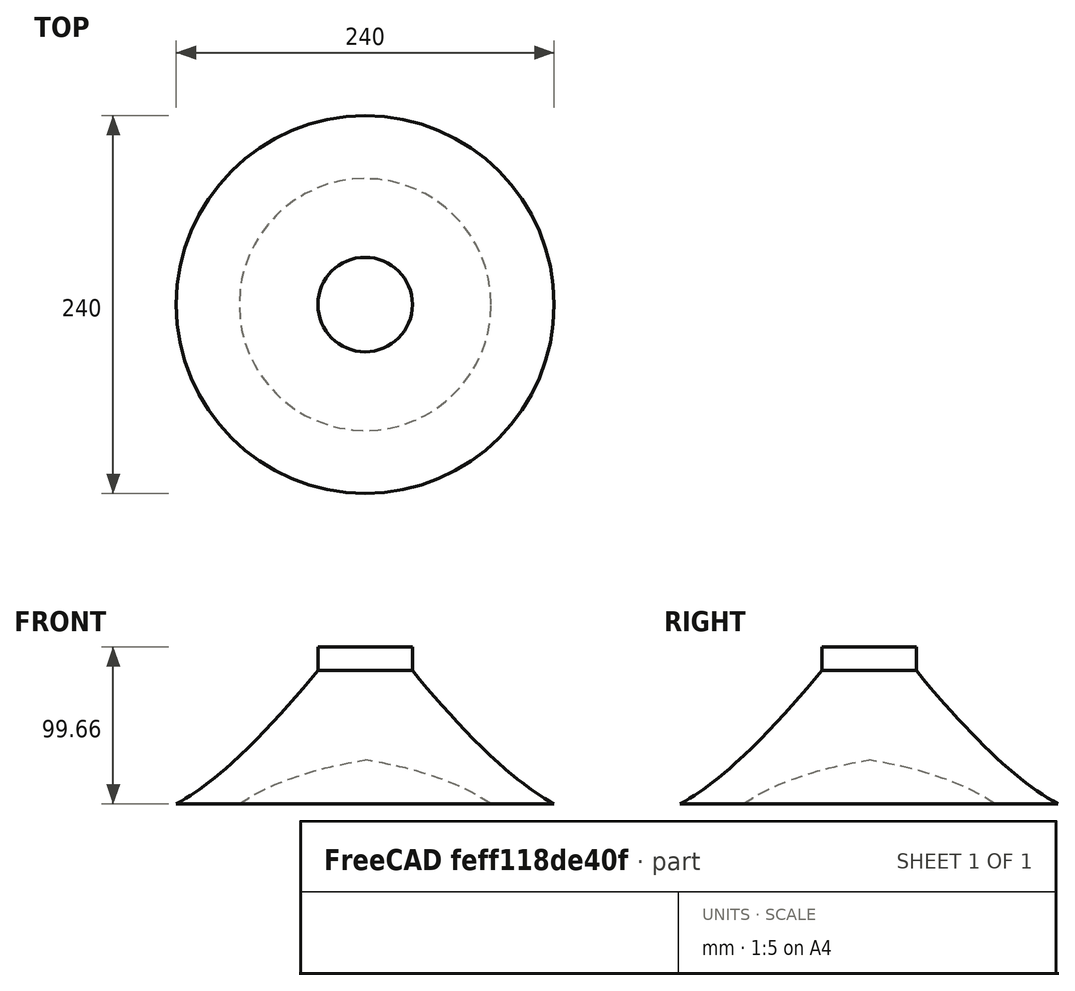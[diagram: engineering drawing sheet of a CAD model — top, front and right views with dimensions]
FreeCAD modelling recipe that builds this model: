
FCSTD DOCUMENT  (FreeCAD 0.20R29410 (Git))
Label: parte_baixo_1
License: All rights reserved
LicenseURL: http://en.wikipedia.org/wiki/All_rights_reserved
objects: Sketcher::SketchObject×1, PartDesign::Revolution×1, PartDesign::Body×1
note: 4 computed .brp shape members not serialized (recipe doc carries the construction recipe); baked Part::Feature solids carry a one-line shape summary decoded from their .brp

FEATURE [Sketcher::SketchObject] Sketch
  FullyConstrained = false
  MapMode = 5
  Placement = pos=(0,0,0) rot=(0.57735,0.57735,0.57735;2.0944rad)
  Support = -> [YZ_Plane]
  sketch-geometry (16):
    g0: Circle CenterX=30 CenterY=84.6645 CenterZ=0 NormalX=0 NormalY=0 NormalZ=1 AngleXU=0 Radius=1
    g1: Circle CenterX=83.0365 CenterY=20 CenterZ=0 NormalX=0 NormalY=0 NormalZ=1 AngleXU=0 Radius=1
    g2: Circle CenterX=120 CenterY=0 CenterZ=0 NormalX=0 NormalY=0 NormalZ=1 AngleXU=0 Radius=1
    g3: BSplineCurve PolesCount=3 KnotsCount=2 Degree=2 IsPeriodic=0
    g4: GeomPoint X=30 Y=84.6645 Z=0
    g5: GeomPoint X=120 Y=0 Z=0
    g6: Circle CenterX=80 CenterY=0 CenterZ=0 NormalX=0 NormalY=0 NormalZ=1 AngleXU=0 Radius=1
    g7: Circle CenterX=50 CenterY=20 CenterZ=0 NormalX=0 NormalY=0 NormalZ=1 AngleXU=0 Radius=1
    g8: Circle CenterX=0 CenterY=27.7845 CenterZ=0 NormalX=0 NormalY=0 NormalZ=1 AngleXU=0 Radius=1
    g9: BSplineCurve PolesCount=3 KnotsCount=2 Degree=2 IsPeriodic=0
    g10: GeomPoint X=80 Y=0 Z=0
    g11: GeomPoint X=0 Y=27.7845 Z=0
    g12: LineSegment StartX=120 StartY=0 StartZ=0 EndX=80 EndY=0 EndZ=0
    g13: LineSegment StartX=0 StartY=99.6645 StartZ=0 EndX=0 EndY=27.7845 EndZ=0
    g14: LineSegment StartX=30 StartY=84.6645 StartZ=0 EndX=30 EndY=99.6645 EndZ=0
    g15: LineSegment StartX=30 StartY=99.6645 StartZ=0 EndX=0 EndY=99.6645 EndZ=0
  constraints (31):
    c: PointOnObject(g3,g-1)
    c: PointOnObject(g13,g-2)
    c: Weight(g0) = 1
    c: Equal(g0,g1)
    c: Equal(g0,g2)
    c: InternalAlignment(g0,g3)
    c: InternalAlignment(g1,g3)
    c: InternalAlignment(g2,g3)
    c: InternalAlignment(g4,g3)
    c: InternalAlignment(g5,g3)
    c: Weight(g6) = 1
    c: Equal(g6,g7)
    c: Equal(g6,g8)
    c: InternalAlignment(g6,g9)
    c: InternalAlignment(g7,g9)
    c: InternalAlignment(g8,g9)
    c: InternalAlignment(g10,g9)
    c: InternalAlignment(g11,g9)
    c: Coincident(g12,g3)
    c: Horizontal(g12)
    c: Coincident(g13,g9)
    c: Vertical(g13)
    c: Distance(g12) = 40
    c: Coincident(g14,g3)
    c: Vertical(g14)
    c: Coincident(g14,g15)
    c: Coincident(g15,g13)
    c: Horizontal(g15)
    c: Distance(g14) = 15
    c: Distance(g15) = 30
    c: Distance(g13) = 71.88
FEATURE [PartDesign::Revolution] Revolution
  Angle = 360
  Axis = (-2e-16,3e-16,1)
  Base = (0,0,0)
  Placement = pos=(0,0,0) rot=(0.57735,0.57735,0.57735;2.0944rad)
  Profile = -> Sketch
  ReferenceAxis = -> Sketch [V_Axis]
  Reversed = true
FEATURE [PartDesign::Body] Body
  Group = -> [Sketch,Revolution]
  Origin = -> Origin
  Tip = -> Revolution
